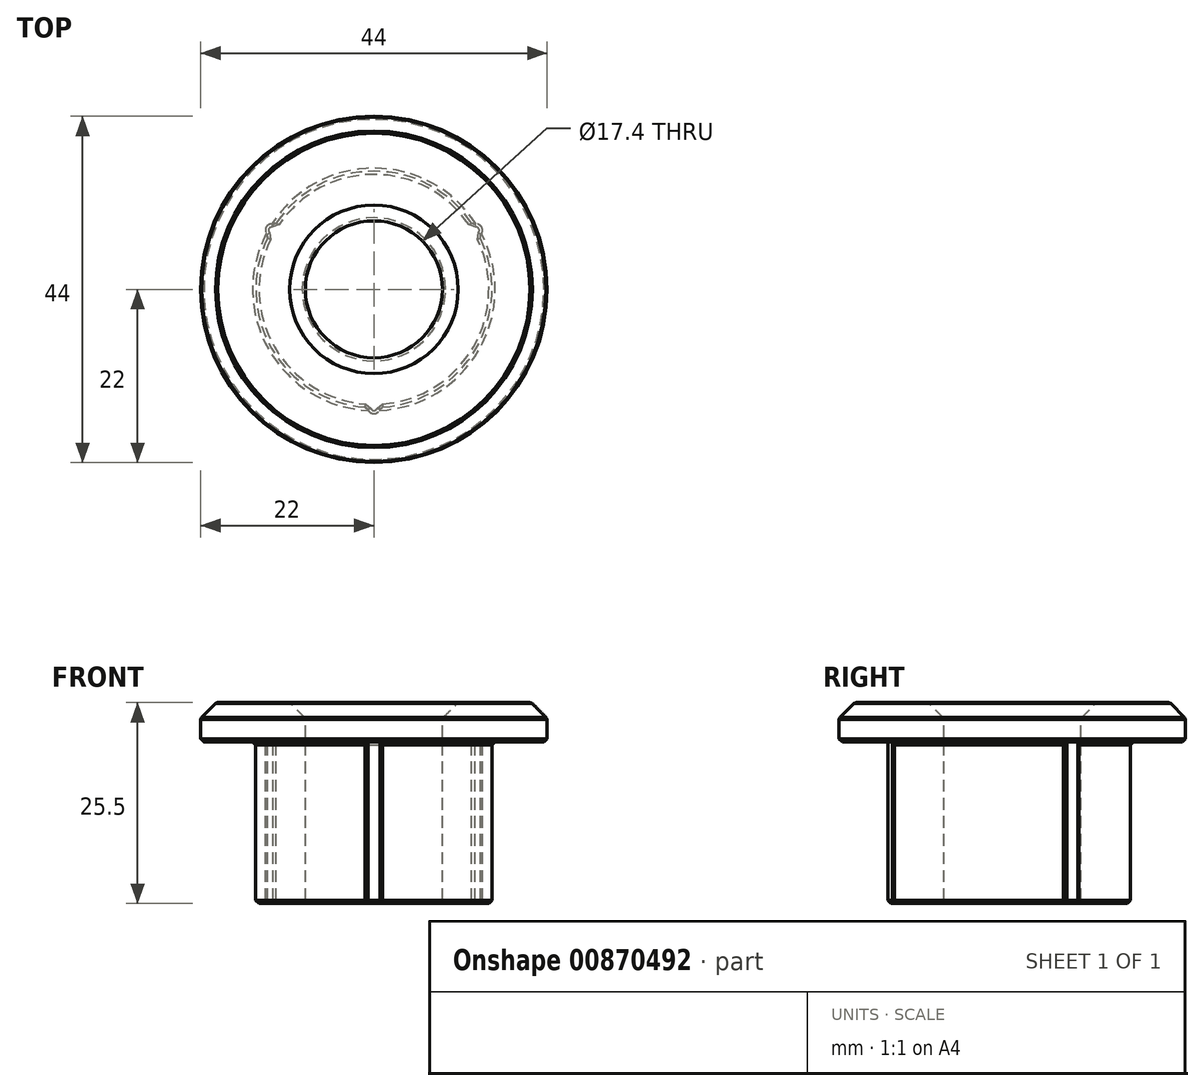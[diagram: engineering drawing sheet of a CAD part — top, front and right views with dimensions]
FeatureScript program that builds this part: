
annotation { "Feature Type Name" : "Feature", "Feature Type Description" : "" }
export const myFeature = defineFeature(function(context is Context, id is Id, definition is map)
    precondition{}
    {
        {
            var Q0;
            Q0=qCreatedBy(makeId("Front.planeOp"),FACE);
            var sketch = newSketch(context, id + "F0", { "sketchPlane" : qUnion([Q0])});
            skLineSegment(sketch, "E0", {"start": v(-8.7, 0) * mm, "end": v(-8.7, 25.5) * mm});
            skLineSegment(sketch, "E1", {"start": v(-8.7, 25.5) * mm, "end": v(-20, 25.5) * mm});
            skLineSegment(sketch, "E2", {"start": v(-20, 25.5) * mm, "end": v(-22, 23.5) * mm});
            skLineSegment(sketch, "E3", {"start": v(-22, 23.5) * mm, "end": v(-22, 20.5) * mm});
            skLineSegment(sketch, "E4", {"start": v(-22, 20.5) * mm, "end": v(-15, 20.5) * mm});
            skLineSegment(sketch, "E5", {"start": v(-15, 20.5) * mm, "end": v(-15, 0) * mm});
            skLineSegment(sketch, "E6", {"start": v(-15, 0) * mm, "end": v(-8.7, 0) * mm});
            skLineSegment(sketch, "E7", {"start": v(0, 25.5) * mm, "end": v(0, 0) * mm, "construction": true});
            skSolve(sketch);
        }
        {
            var Q0;
            Q0=makeQuery(id+"F0.imprint","IMPRINT",FACE,{"disambiguationData":[TD([[makeQuery(id+"F0.imprint","IMPRINT",EDGE,{"derivedFrom":sQuery(id+"F0.wireOp",EDGE,"E0")}),1.0]])]});
            var Q1;
            Q1=sQuery(id+"F0.wireOp",EDGE,"E7");
            revolve(context, id + "F1", {"surfaceOperationType" : NewSurfaceOperationType.NEW, "entities" : qUnion([Q0]), "axis" : qUnion([Q1]), "revolveType" : RevolveType.FULL});
        }
        {
            var Q0;
            Q0=makeQuery(id+"F1.opRevolve","SWEPT_FACE",FACE,{"disambiguationData":[OSD([sQuery(id+"F0.wireOp",EDGE,"E4")])]});
            var sketch = newSketch(context, id + "F2", { "sketchPlane" : qUnion([Q0])});
            skCircle(sketch, "E8", {"center": v(0, 15) * mm, "radius": 0.8 * mm});
            skCircle(sketch, "E9.1.0", {"center": v(-13, -7.5) * mm, "radius": 0.8 * mm});
            skCircle(sketch, "E9.2.0", {"center": v(13, -7.5) * mm, "radius": 0.8 * mm});
            skPoint(sketch, "E9.center", {"position": v(0, 0) * mm});
            skCircle(sketch, "E10", {"center": v(0, 0) * mm, "radius": 15.8 * mm, "construction": true});
            skSolve(sketch);
        }
        {
            var Q0;
            {var subQ0=sQuery(id+"F2.wireOp",EDGE,"E8");var subQ1=makeQuery(id+"F1.opRevolve","SWEPT_EDGE",EDGE,{"disambiguationData":[OSD([sQuery(id+"F0.wireOp",EDGE,"E4"),sQuery(id+"F0.wireOp",EDGE,"E5")])]});var subQ2=makeQuery(id+"F2.imprint","INTERSECT",VERTEX,{"disambiguationData":[OD(0.0)],"derivedFrom":[subQ1,subQ0]});Q0=makeQuery(id+"F2.imprint","IMPRINT",FACE,{"disambiguationData":[TD([[makeQuery(id+"F2.imprint","IMPRINT",EDGE,{"disambiguationData":[TD([[subQ2,1.0]])],"derivedFrom":subQ0}),1.0]])]});}
            var Q1;
            {var subQ0=sQuery(id+"F2.wireOp",EDGE,"E9.1.0");var subQ1=makeQuery(id+"F1.opRevolve","SWEPT_EDGE",EDGE,{"disambiguationData":[OSD([sQuery(id+"F0.wireOp",EDGE,"E4"),sQuery(id+"F0.wireOp",EDGE,"E5")])]});var subQ2=makeQuery(id+"F2.imprint","INTERSECT",VERTEX,{"disambiguationData":[OD(0.0)],"derivedFrom":[subQ1,subQ0]});Q1=makeQuery(id+"F2.imprint","IMPRINT",FACE,{"disambiguationData":[TD([[makeQuery(id+"F2.imprint","IMPRINT",EDGE,{"disambiguationData":[TD([[subQ2,-1.0]])],"derivedFrom":subQ0}),1.0]])]});}
            var Q2;
            {var subQ0=sQuery(id+"F2.wireOp",EDGE,"E9.2.0");var subQ1=makeQuery(id+"F1.opRevolve","SWEPT_EDGE",EDGE,{"disambiguationData":[OSD([sQuery(id+"F0.wireOp",EDGE,"E4"),sQuery(id+"F0.wireOp",EDGE,"E5")])]});var subQ2=makeQuery(id+"F2.imprint","INTERSECT",VERTEX,{"disambiguationData":[OD(0.0)],"derivedFrom":[subQ1,subQ0]});Q2=makeQuery(id+"F2.imprint","IMPRINT",FACE,{"disambiguationData":[TD([[makeQuery(id+"F2.imprint","IMPRINT",EDGE,{"disambiguationData":[TD([[subQ2,-1.0]])],"derivedFrom":subQ0}),1.0]])]});}
            var Q3;
            Q3=makeQuery(id+"F1.opRevolve","SWEPT_FACE",FACE,{"disambiguationData":[OSD([sQuery(id+"F0.wireOp",EDGE,"E6")])]});
            extrude(context, id + "F3", {"entities" : qUnion([Q0, Q1, Q2]), "operationType" : NewBodyOperationType.ADD, "endBound" : BoundingType.UP_TO_SURFACE, "depth" : 25 * mm, "endBoundEntityFace" : qUnion([Q3]), "offsetDistance" : 25 * mm});
        }
        {
            var Q0;
            Q0=makeQuery(id+"F1.opRevolve","SWEPT_EDGE",EDGE,{"disambiguationData":[OSD([sQuery(id+"F0.wireOp",EDGE,"E0"),sQuery(id+"F0.wireOp",EDGE,"E6")])]});
            var Q1;
            {var subQ0=sQuery(id+"F0.wireOp",EDGE,"E5");var subQ1=sQuery(id+"F0.wireOp",EDGE,"E6");Q1=makeQuery(id+"F3.boolean.opBoolean","SPLIT",EDGE,{"disambiguationData":[TD([makeQuery(id+"F1.opRevolve","SWEPT_FACE",FACE,{"disambiguationData":[OSD([subQ0])]}),makeQuery(id+"F1.opRevolve","SWEPT_FACE",FACE,{"disambiguationData":[OSD([subQ1])]}),makeQuery(id+"F3.opExtrude","SWEPT_FACE",FACE,{"disambiguationData":[OSD([sQuery(id+"F2.wireOp",EDGE,"E9.1.0")])]}),makeQuery(id+"F3.opExtrude","SWEPT_FACE",FACE,{"disambiguationData":[OSD([sQuery(id+"F2.wireOp",EDGE,"E9.2.0")])]}),makeQuery(id+"F3.opExtrude","CAP_FACE",FACE,{"disambiguationData":[OSD([subQ1]),OD(0.0)],"isStart":false}),makeQuery(id+"F3.opExtrude","CAP_FACE",FACE,{"disambiguationData":[OSD([subQ1]),OD(1.0)],"isStart":false}),makeQuery(id+"F3.opExtrude","CAP_FACE",FACE,{"disambiguationData":[OSD([subQ1]),OD(2.0)],"isStart":false})])],"derivedFrom":makeQuery(id+"F1.opRevolve","SWEPT_EDGE",EDGE,{"disambiguationData":[OSD([subQ0,subQ1])]})});}
            var Q2;
            {var subQ0=sQuery(id+"F2.wireOp",EDGE,"E9.1.0");var subQ1=makeQuery(id+"F1.opRevolve","SWEPT_EDGE",EDGE,{"disambiguationData":[OSD([sQuery(id+"F0.wireOp",EDGE,"E4"),sQuery(id+"F0.wireOp",EDGE,"E5")])]});Q2=makeQuery(id+"F3.opExtrude","TWEAK_EDGE",EDGE,{"derivedFrom":[makeQuery(id+"F1.opRevolve","SWEPT_FACE",FACE,{"disambiguationData":[OSD([sQuery(id+"F0.wireOp",EDGE,"E6")])]}),makeQuery(id+"F2.imprint","IMPRINT",EDGE,{"disambiguationData":[TD([[makeQuery(id+"F2.imprint","INTERSECT",VERTEX,{"disambiguationData":[OD(0.0)],"derivedFrom":[subQ1,subQ0]}),-1.0]])],"derivedFrom":subQ0})]});}
            var Q3;
            {var subQ0=sQuery(id+"F0.wireOp",EDGE,"E6");var subQ1=sQuery(id+"F0.wireOp",EDGE,"E5");Q3=makeQuery(id+"F3.boolean.opBoolean","SPLIT",EDGE,{"disambiguationData":[TD([makeQuery(id+"F1.opRevolve","SWEPT_FACE",FACE,{"disambiguationData":[OSD([subQ1])]}),makeQuery(id+"F1.opRevolve","SWEPT_FACE",FACE,{"disambiguationData":[OSD([subQ0])]}),makeQuery(id+"F3.opExtrude","SWEPT_FACE",FACE,{"disambiguationData":[OSD([sQuery(id+"F2.wireOp",EDGE,"E8")])]}),makeQuery(id+"F3.opExtrude","SWEPT_FACE",FACE,{"disambiguationData":[OSD([sQuery(id+"F2.wireOp",EDGE,"E9.1.0")])]}),makeQuery(id+"F3.opExtrude","CAP_FACE",FACE,{"disambiguationData":[OSD([subQ0]),OD(0.0)],"isStart":false}),makeQuery(id+"F3.opExtrude","CAP_FACE",FACE,{"disambiguationData":[OSD([subQ0]),OD(1.0)],"isStart":false}),makeQuery(id+"F3.opExtrude","CAP_FACE",FACE,{"disambiguationData":[OSD([subQ0]),OD(2.0)],"isStart":false})])],"derivedFrom":makeQuery(id+"F1.opRevolve","SWEPT_EDGE",EDGE,{"disambiguationData":[OSD([subQ1,subQ0])]})});}
            var Q4;
            {var subQ0=sQuery(id+"F2.wireOp",EDGE,"E8");var subQ1=makeQuery(id+"F1.opRevolve","SWEPT_EDGE",EDGE,{"disambiguationData":[OSD([sQuery(id+"F0.wireOp",EDGE,"E4"),sQuery(id+"F0.wireOp",EDGE,"E5")])]});Q4=makeQuery(id+"F3.opExtrude","TWEAK_EDGE",EDGE,{"derivedFrom":[makeQuery(id+"F1.opRevolve","SWEPT_FACE",FACE,{"disambiguationData":[OSD([sQuery(id+"F0.wireOp",EDGE,"E6")])]}),makeQuery(id+"F2.imprint","IMPRINT",EDGE,{"disambiguationData":[TD([[makeQuery(id+"F2.imprint","INTERSECT",VERTEX,{"disambiguationData":[OD(0.0)],"derivedFrom":[subQ1,subQ0]}),1.0]])],"derivedFrom":subQ0})]});}
            var Q5;
            {var subQ0=sQuery(id+"F0.wireOp",EDGE,"E5");var subQ1=sQuery(id+"F0.wireOp",EDGE,"E6");Q5=makeQuery(id+"F3.boolean.opBoolean","SPLIT",EDGE,{"disambiguationData":[TD([makeQuery(id+"F1.opRevolve","SWEPT_FACE",FACE,{"disambiguationData":[OSD([subQ0])]}),makeQuery(id+"F1.opRevolve","SWEPT_FACE",FACE,{"disambiguationData":[OSD([subQ1])]}),makeQuery(id+"F3.opExtrude","SWEPT_FACE",FACE,{"disambiguationData":[OSD([sQuery(id+"F2.wireOp",EDGE,"E8")])]}),makeQuery(id+"F3.opExtrude","SWEPT_FACE",FACE,{"disambiguationData":[OSD([sQuery(id+"F2.wireOp",EDGE,"E9.2.0")])]}),makeQuery(id+"F3.opExtrude","CAP_FACE",FACE,{"disambiguationData":[OSD([subQ1]),OD(0.0)],"isStart":false}),makeQuery(id+"F3.opExtrude","CAP_FACE",FACE,{"disambiguationData":[OSD([subQ1]),OD(1.0)],"isStart":false}),makeQuery(id+"F3.opExtrude","CAP_FACE",FACE,{"disambiguationData":[OSD([subQ1]),OD(2.0)],"isStart":false})])],"derivedFrom":makeQuery(id+"F1.opRevolve","SWEPT_EDGE",EDGE,{"disambiguationData":[OSD([subQ0,subQ1])]})});}
            var Q6;
            {var subQ0=sQuery(id+"F2.wireOp",EDGE,"E9.2.0");var subQ1=makeQuery(id+"F1.opRevolve","SWEPT_EDGE",EDGE,{"disambiguationData":[OSD([sQuery(id+"F0.wireOp",EDGE,"E4"),sQuery(id+"F0.wireOp",EDGE,"E5")])]});Q6=makeQuery(id+"F3.opExtrude","TWEAK_EDGE",EDGE,{"derivedFrom":[makeQuery(id+"F1.opRevolve","SWEPT_FACE",FACE,{"disambiguationData":[OSD([sQuery(id+"F0.wireOp",EDGE,"E6")])]}),makeQuery(id+"F2.imprint","IMPRINT",EDGE,{"disambiguationData":[TD([[makeQuery(id+"F2.imprint","INTERSECT",VERTEX,{"disambiguationData":[OD(0.0)],"derivedFrom":[subQ1,subQ0]}),-1.0]])],"derivedFrom":subQ0})]});}
            var Q7;
            Q7=makeQuery(id+"F1.opRevolve","SWEPT_EDGE",EDGE,{"disambiguationData":[OSD([sQuery(id+"F0.wireOp",EDGE,"E3"),sQuery(id+"F0.wireOp",EDGE,"E4")])]});
            var Q8;
            {var subQ0=sQuery(id+"F0.wireOp",EDGE,"E4");var subQ1=sQuery(id+"F0.wireOp",EDGE,"E5");Q8=makeQuery(id+"F3.boolean.opBoolean","SPLIT",EDGE,{"disambiguationData":[TD([makeQuery(id+"F1.opRevolve","SWEPT_FACE",FACE,{"disambiguationData":[OSD([subQ0])]}),makeQuery(id+"F1.opRevolve","SWEPT_FACE",FACE,{"disambiguationData":[OSD([subQ1])]}),makeQuery(id+"F3.opExtrude","SWEPT_FACE",FACE,{"disambiguationData":[OSD([sQuery(id+"F2.wireOp",EDGE,"E8")])]}),makeQuery(id+"F3.opExtrude","SWEPT_FACE",FACE,{"disambiguationData":[OSD([sQuery(id+"F2.wireOp",EDGE,"E9.1.0")])]})])],"derivedFrom":makeQuery(id+"F1.opRevolve","SWEPT_EDGE",EDGE,{"disambiguationData":[OSD([subQ0,subQ1])]})});}
            var Q9;
            {var subQ0=sQuery(id+"F0.wireOp",EDGE,"E4");var subQ1=sQuery(id+"F0.wireOp",EDGE,"E5");Q9=makeQuery(id+"F3.boolean.opBoolean","SPLIT",EDGE,{"disambiguationData":[TD([makeQuery(id+"F1.opRevolve","SWEPT_FACE",FACE,{"disambiguationData":[OSD([subQ0])]}),makeQuery(id+"F1.opRevolve","SWEPT_FACE",FACE,{"disambiguationData":[OSD([subQ1])]}),makeQuery(id+"F3.opExtrude","SWEPT_FACE",FACE,{"disambiguationData":[OSD([sQuery(id+"F2.wireOp",EDGE,"E8")])]}),makeQuery(id+"F3.opExtrude","SWEPT_FACE",FACE,{"disambiguationData":[OSD([sQuery(id+"F2.wireOp",EDGE,"E9.2.0")])]})])],"derivedFrom":makeQuery(id+"F1.opRevolve","SWEPT_EDGE",EDGE,{"disambiguationData":[OSD([subQ0,subQ1])]})});}
            var Q10;
            {var subQ0=sQuery(id+"F0.wireOp",EDGE,"E4");var subQ1=sQuery(id+"F0.wireOp",EDGE,"E5");Q10=makeQuery(id+"F3.boolean.opBoolean","SPLIT",EDGE,{"disambiguationData":[TD([makeQuery(id+"F1.opRevolve","SWEPT_FACE",FACE,{"disambiguationData":[OSD([subQ0])]}),makeQuery(id+"F1.opRevolve","SWEPT_FACE",FACE,{"disambiguationData":[OSD([subQ1])]}),makeQuery(id+"F3.opExtrude","SWEPT_FACE",FACE,{"disambiguationData":[OSD([sQuery(id+"F2.wireOp",EDGE,"E9.1.0")])]}),makeQuery(id+"F3.opExtrude","SWEPT_FACE",FACE,{"disambiguationData":[OSD([sQuery(id+"F2.wireOp",EDGE,"E9.2.0")])]})])],"derivedFrom":makeQuery(id+"F1.opRevolve","SWEPT_EDGE",EDGE,{"disambiguationData":[OSD([subQ0,subQ1])]})});}
            var Q11;
            {var subQ0=sQuery(id+"F0.wireOp",EDGE,"E6");Q11=makeQuery(id+"F3.boolean.opBoolean","SPLIT",FACE,{"disambiguationData":[TD([makeQuery(id+"F1.opRevolve","SWEPT_FACE",FACE,{"disambiguationData":[OSD([sQuery(id+"F0.wireOp",EDGE,"E4")])]}),makeQuery(id+"F1.opRevolve","SWEPT_FACE",FACE,{"disambiguationData":[OSD([subQ0])]}),makeQuery(id+"F3.opExtrude","SWEPT_FACE",FACE,{"disambiguationData":[OSD([sQuery(id+"F2.wireOp",EDGE,"E9.1.0")])]}),makeQuery(id+"F3.opExtrude","SWEPT_FACE",FACE,{"disambiguationData":[OSD([sQuery(id+"F2.wireOp",EDGE,"E9.2.0")])]}),makeQuery(id+"F3.opExtrude","CAP_FACE",FACE,{"disambiguationData":[OSD([subQ0]),OD(0.0)],"isStart":false}),makeQuery(id+"F3.opExtrude","CAP_FACE",FACE,{"disambiguationData":[OSD([subQ0]),OD(1.0)],"isStart":false}),makeQuery(id+"F3.opExtrude","CAP_FACE",FACE,{"disambiguationData":[OSD([subQ0]),OD(2.0)],"isStart":false})])],"derivedFrom":makeQuery(id+"F1.opRevolve","SWEPT_FACE",FACE,{"disambiguationData":[OSD([sQuery(id+"F0.wireOp",EDGE,"E5")])]})});}
            var Q12;
            {var subQ0=sQuery(id+"F0.wireOp",EDGE,"E6");Q12=makeQuery(id+"F3.boolean.opBoolean","SPLIT",FACE,{"disambiguationData":[TD([makeQuery(id+"F1.opRevolve","SWEPT_FACE",FACE,{"disambiguationData":[OSD([sQuery(id+"F0.wireOp",EDGE,"E4")])]}),makeQuery(id+"F1.opRevolve","SWEPT_FACE",FACE,{"disambiguationData":[OSD([subQ0])]}),makeQuery(id+"F3.opExtrude","SWEPT_FACE",FACE,{"disambiguationData":[OSD([sQuery(id+"F2.wireOp",EDGE,"E8")])]}),makeQuery(id+"F3.opExtrude","SWEPT_FACE",FACE,{"disambiguationData":[OSD([sQuery(id+"F2.wireOp",EDGE,"E9.1.0")])]}),makeQuery(id+"F3.opExtrude","CAP_FACE",FACE,{"disambiguationData":[OSD([subQ0]),OD(0.0)],"isStart":false}),makeQuery(id+"F3.opExtrude","CAP_FACE",FACE,{"disambiguationData":[OSD([subQ0]),OD(1.0)],"isStart":false}),makeQuery(id+"F3.opExtrude","CAP_FACE",FACE,{"disambiguationData":[OSD([subQ0]),OD(2.0)],"isStart":false})])],"derivedFrom":makeQuery(id+"F1.opRevolve","SWEPT_FACE",FACE,{"disambiguationData":[OSD([sQuery(id+"F0.wireOp",EDGE,"E5")])]})});}
            var Q13;
            {var subQ0=sQuery(id+"F0.wireOp",EDGE,"E6");Q13=makeQuery(id+"F3.boolean.opBoolean","SPLIT",FACE,{"disambiguationData":[TD([makeQuery(id+"F1.opRevolve","SWEPT_FACE",FACE,{"disambiguationData":[OSD([sQuery(id+"F0.wireOp",EDGE,"E4")])]}),makeQuery(id+"F1.opRevolve","SWEPT_FACE",FACE,{"disambiguationData":[OSD([subQ0])]}),makeQuery(id+"F3.opExtrude","SWEPT_FACE",FACE,{"disambiguationData":[OSD([sQuery(id+"F2.wireOp",EDGE,"E8")])]}),makeQuery(id+"F3.opExtrude","SWEPT_FACE",FACE,{"disambiguationData":[OSD([sQuery(id+"F2.wireOp",EDGE,"E9.2.0")])]}),makeQuery(id+"F3.opExtrude","CAP_FACE",FACE,{"disambiguationData":[OSD([subQ0]),OD(0.0)],"isStart":false}),makeQuery(id+"F3.opExtrude","CAP_FACE",FACE,{"disambiguationData":[OSD([subQ0]),OD(1.0)],"isStart":false}),makeQuery(id+"F3.opExtrude","CAP_FACE",FACE,{"disambiguationData":[OSD([subQ0]),OD(2.0)],"isStart":false})])],"derivedFrom":makeQuery(id+"F1.opRevolve","SWEPT_FACE",FACE,{"disambiguationData":[OSD([sQuery(id+"F0.wireOp",EDGE,"E5")])]})});}
            var Q14;
            Q14=makeQuery(id+"F1.opRevolve","SWEPT_EDGE",EDGE,{"disambiguationData":[OSD([sQuery(id+"F0.wireOp",EDGE,"E1"),sQuery(id+"F0.wireOp",EDGE,"E2")])]});
            var Q15;
            Q15=makeQuery(id+"F1.opRevolve","SWEPT_EDGE",EDGE,{"disambiguationData":[OSD([sQuery(id+"F0.wireOp",EDGE,"E2"),sQuery(id+"F0.wireOp",EDGE,"E3")])]});
            chamfer(context, id + "F4", {"entities" : qUnion([Q0, Q1, Q2, Q3, Q4, Q5, Q6, Q7, Q8, Q9, Q10, Q11, Q12, Q13, Q14, Q15]), "width" : 0.4 * mm, "tangentPropagation" : true});
        }
        {
            var Q0;
            Q0=makeQuery(id+"F1.opRevolve","SWEPT_EDGE",EDGE,{"disambiguationData":[OSD([sQuery(id+"F0.wireOp",EDGE,"E0"),sQuery(id+"F0.wireOp",EDGE,"E1")])]});
            chamfer(context, id + "F5", {"entities" : qUnion([Q0]), "width" : 2 * mm, "tangentPropagation" : true});
        }
    });
